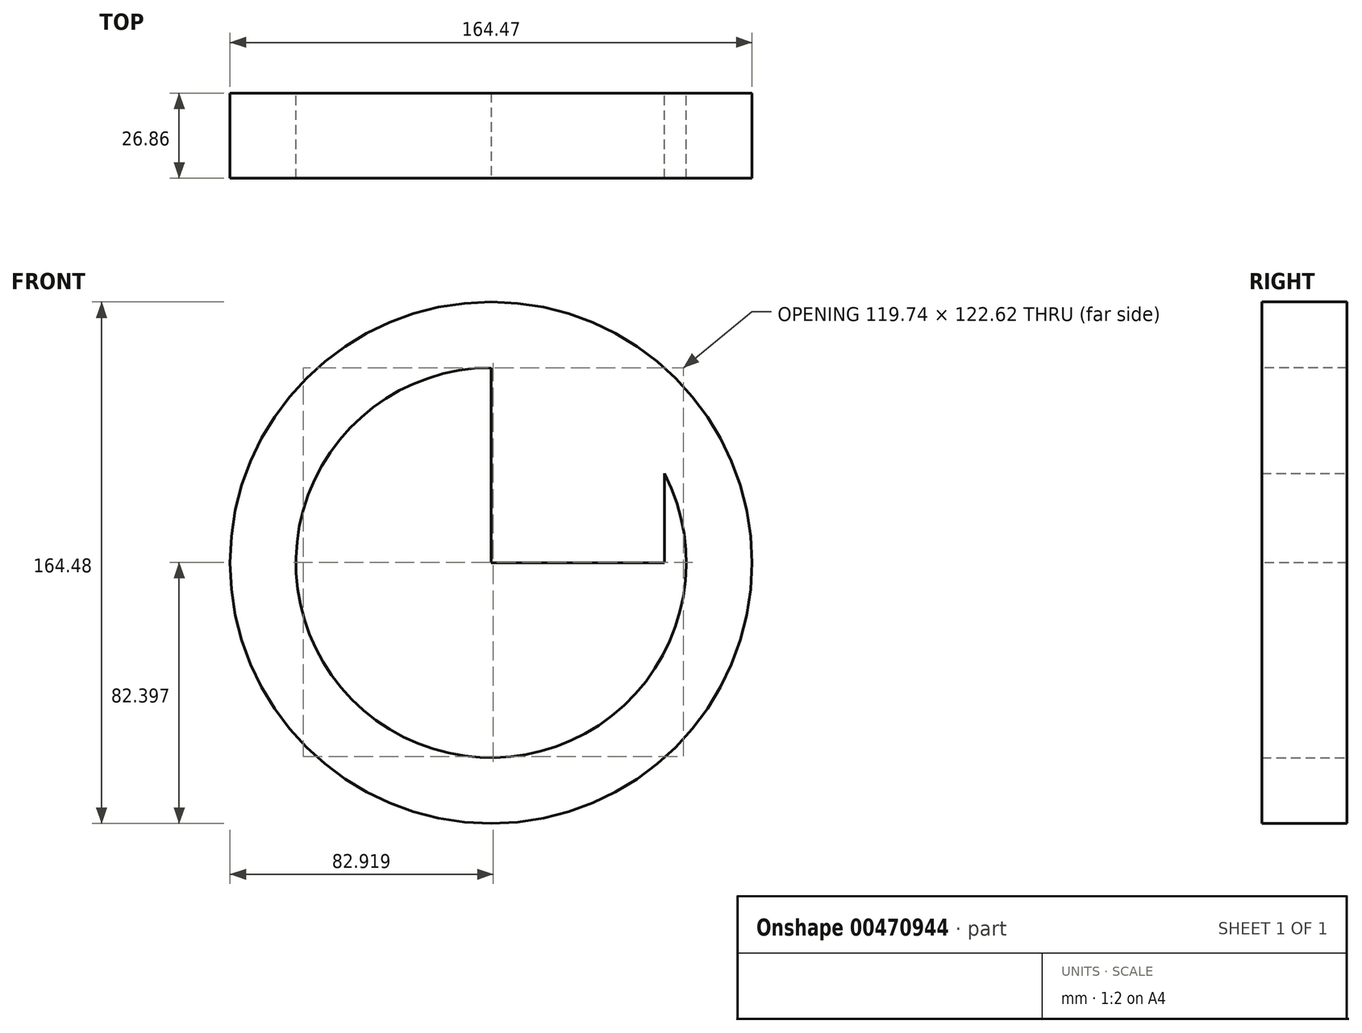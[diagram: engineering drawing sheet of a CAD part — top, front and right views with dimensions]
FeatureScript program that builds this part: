
annotation { "Feature Type Name" : "Feature", "Feature Type Description" : "" }
export const myFeature = defineFeature(function(context is Context, id is Id, definition is map)
    precondition{}
    {
        {
            var Q0;
            Q0=qCreatedBy(makeId("Top.planeOp"),FACE);
            var sketch = newSketch(context, id + "F0", { "sketchPlane" : qUnion([Q0])});
            skLineSegment(sketch, "E0.bottom", {"start": v(0, 0) * mm, "end": v(-54.63, 0) * mm});
            skLineSegment(sketch, "E0.top", {"start": v(0, -26.86) * mm, "end": v(-54.63, -26.86) * mm});
            skLineSegment(sketch, "E0.left", {"start": v(0, 0) * mm, "end": v(0, -26.86) * mm});
            skLineSegment(sketch, "E0.right", {"start": v(-54.63, 0) * mm, "end": v(-54.63, -26.86) * mm});
            skSolve(sketch);
        }
        {
            var Q0;
            Q0 = qSketchRegion(id + "F0", true);
            extrude(context, id + "F1", {"entities" : qUnion([Q0]), "depth" : 61.47 * mm});
        }
        {
            var Q0;
            Q0=makeQuery(id+"F1.opExtrude","CAP_FACE",FACE,{"disambiguationData":[OSD([sQuery(id+"F0.wireOp",EDGE,"E0.bottom"),sQuery(id+"F0.wireOp",EDGE,"E0.top"),sQuery(id+"F0.wireOp",EDGE,"E0.left"),sQuery(id+"F0.wireOp",EDGE,"E0.right")])],"isStart":false});
            var Q1;
            Q1=makeQuery(id+"F1.opExtrude","CAP_EDGE",EDGE,{"disambiguationData":[OSD([sQuery(id+"F0.wireOp",EDGE,"E0.right")])],"isStart":true});
            revolve(context, id + "F2", {"operationType" : NewBodyOperationType.ADD, "entities" : qUnion([Q0]), "axis" : qUnion([Q1]), "revolveType" : RevolveType.FULL});
        }
    });
